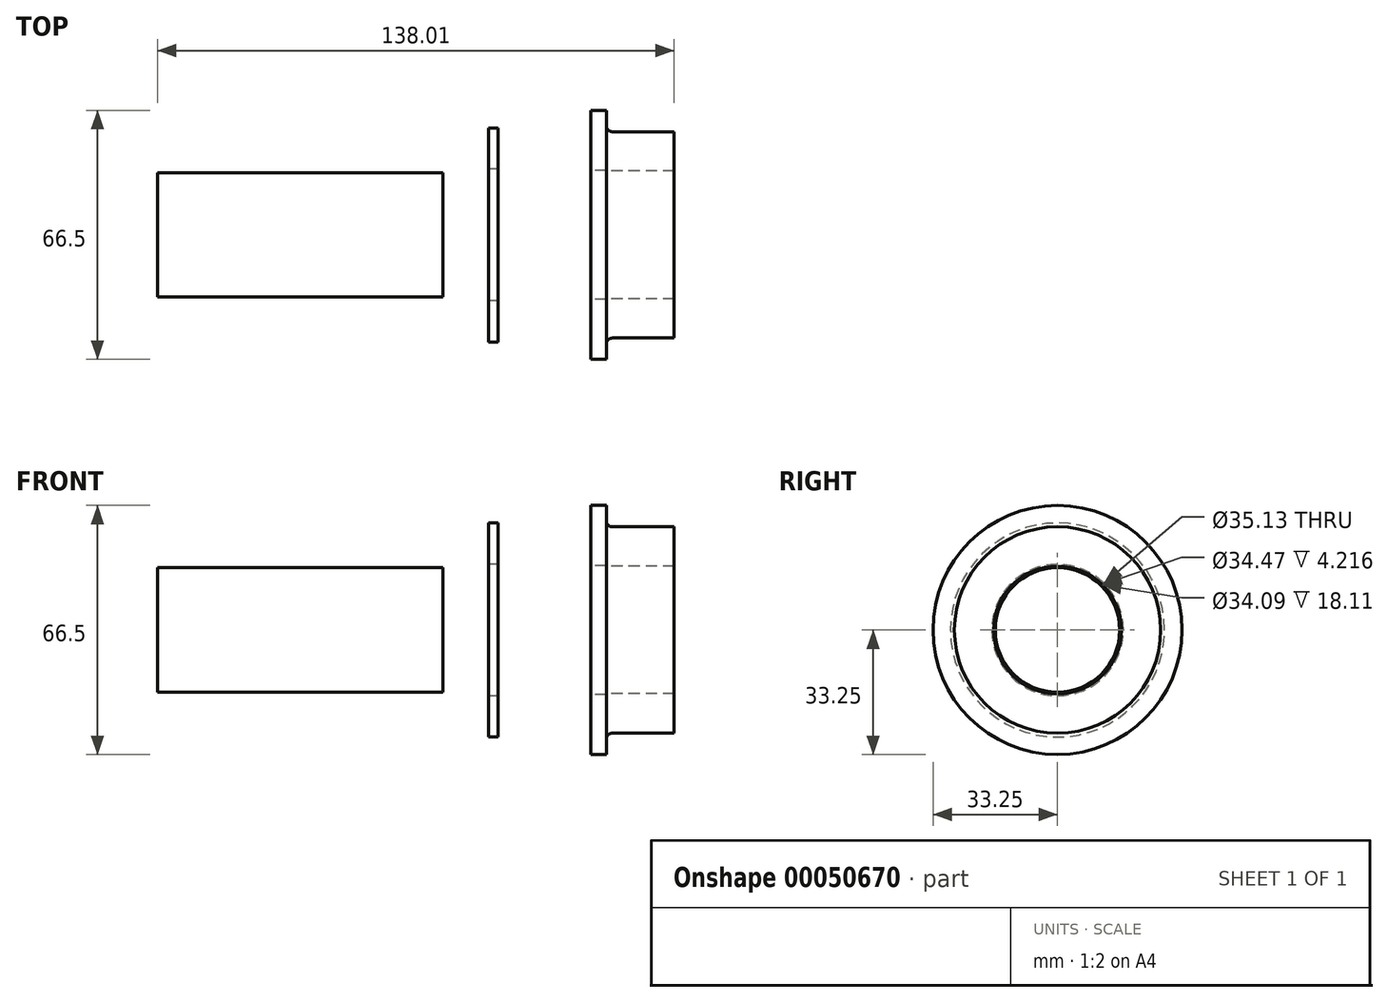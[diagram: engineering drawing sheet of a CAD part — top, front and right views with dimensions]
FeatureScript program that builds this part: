
annotation { "Feature Type Name" : "Feature", "Feature Type Description" : "" }
export const myFeature = defineFeature(function(context is Context, id is Id, definition is map)
    precondition{}
    {
        {
            var Q0;
            Q0=qCreatedBy(makeId("Top.planeOp"),FACE);
            var sketch = newSketch(context, id + "F0", { "sketchPlane" : qUnion([Q0])});
            skLineSegment(sketch, "E0", {"start": v(-111.1, 0) * mm, "end": v(111.82, 0) * mm, "construction": true});
            skLineSegment(sketch, "E1.bottom", {"start": v(-65.37, 0) * mm, "end": v(10.83, 0) * mm});
            skLineSegment(sketch, "E1.top", {"start": v(-65.37, 16.61) * mm, "end": v(10.83, 16.61) * mm});
            skLineSegment(sketch, "E1.left", {"start": v(-65.37, 0) * mm, "end": v(-65.37, 16.61) * mm});
            skLineSegment(sketch, "E1.right", {"start": v(10.83, 0) * mm, "end": v(10.83, 16.61) * mm});
            skLineSegment(sketch, "E2.bottom", {"start": v(23.12, 17.56) * mm, "end": v(25.66, 17.56) * mm});
            skLineSegment(sketch, "E2.top", {"start": v(23.12, 28.58) * mm, "end": v(25.66, 28.58) * mm});
            skLineSegment(sketch, "E2.left", {"start": v(23.12, 17.56) * mm, "end": v(23.12, 28.58) * mm});
            skLineSegment(sketch, "E2.right", {"start": v(25.66, 17.56) * mm, "end": v(25.66, 28.58) * mm});
            skLineSegment(sketch, "E3.bottom", {"start": v(50.32, 17.23) * mm, "end": v(54.53, 17.23) * mm});
            skLineSegment(sketch, "E3.top", {"start": v(50.32, 33.25) * mm, "end": v(54.53, 33.25) * mm});
            skLineSegment(sketch, "E3.left", {"start": v(50.32, 17.23) * mm, "end": v(50.32, 33.25) * mm});
            skLineSegment(sketch, "E3.right", {"start": v(54.53, 29.13) * mm, "end": v(54.53, 33.25) * mm});
            skLineSegment(sketch, "E4.top", {"start": v(56.12, 27.55) * mm, "end": v(72.64, 27.55) * mm});
            skLineSegment(sketch, "E4.right", {"start": v(72.64, 17.23) * mm, "end": v(72.64, 27.55) * mm});
            skLineSegment(sketch, "E5.top", {"start": v(54.53, 17.04) * mm, "end": v(63.04, 17.04) * mm});
            skLineSegment(sketch, "E5.left", {"start": v(54.53, 17.23) * mm, "end": v(54.53, 17.04) * mm});
            skArc(sketch, "E6.filletArc", {"start": v(54.53, 29.13) * mm, "mid": v(55, 28.01) * mm, "end": v(56.12, 27.55) * mm});
            skLineSegment(sketch, "E7", {"start": v(63.04, 17.04) * mm, "end": v(72.64, 17.04) * mm});
            skLineSegment(sketch, "E8", {"start": v(72.64, 17.04) * mm, "end": v(72.64, 17.23) * mm});
            skLineSegment(sketch, "E9", {"start": v(10.83, 16.61) * mm, "end": v(91.22, 16.61) * mm, "construction": true});
            skSolve(sketch);
        }
        {
            var Q0;
            Q0 = qSketchRegion(id + "F0", true);
            var Q1;
            Q1=sQuery(id+"F0.wireOp",EDGE,"E0");
            revolve(context, id + "F1", {"entities" : qUnion([Q0]), "axis" : qUnion([Q1]), "revolveType" : RevolveType.FULL});
        }
    });
